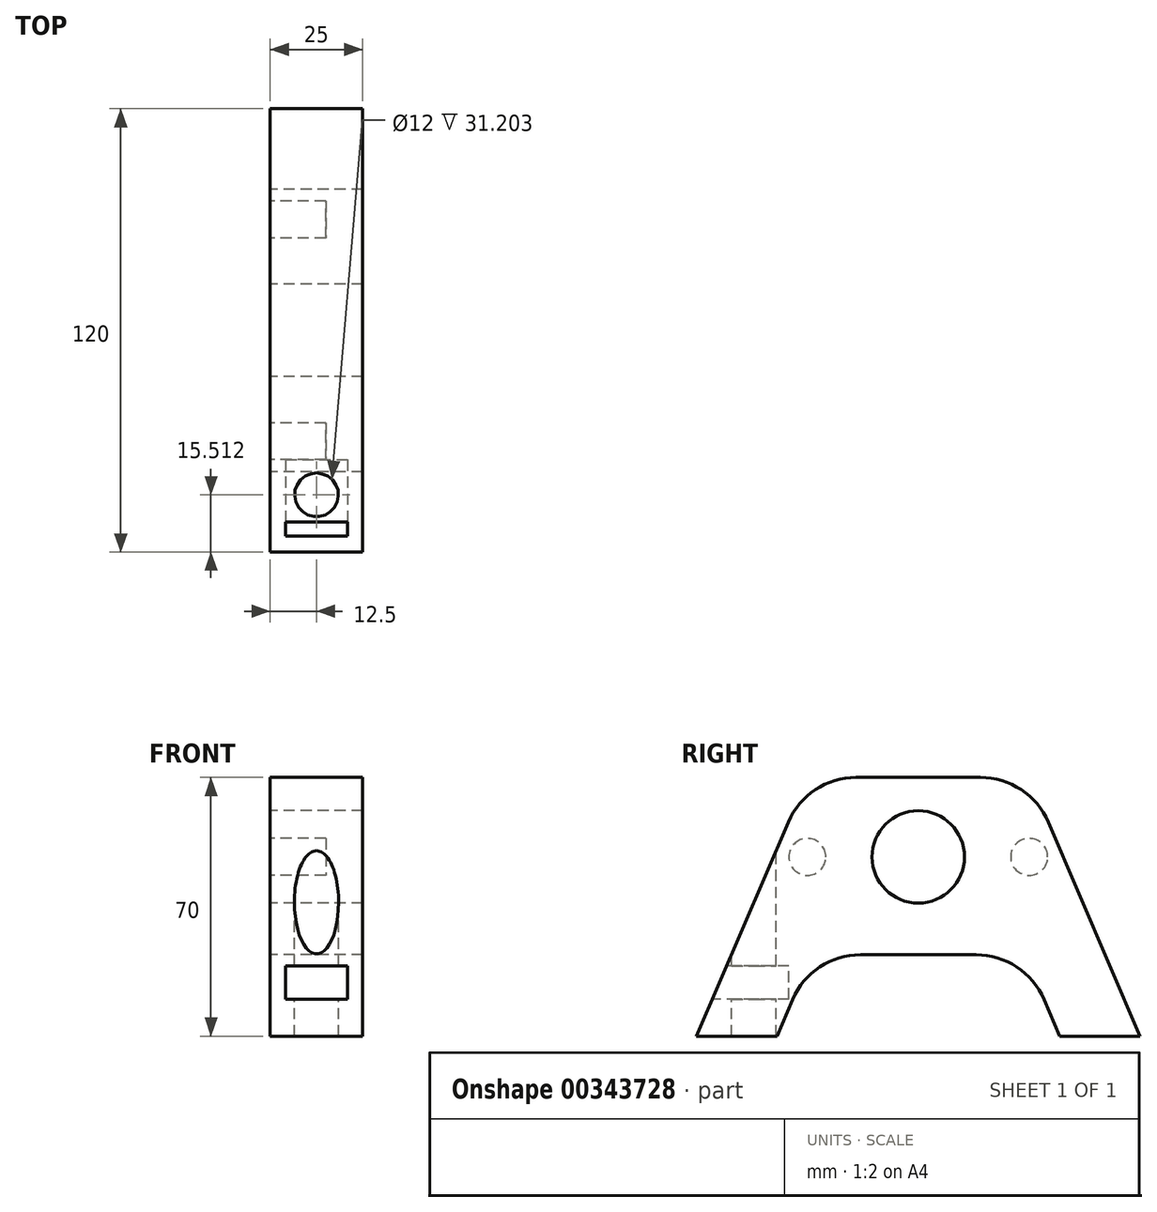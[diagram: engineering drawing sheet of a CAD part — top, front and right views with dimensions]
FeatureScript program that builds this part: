
annotation { "Feature Type Name" : "Feature", "Feature Type Description" : "" }
export const myFeature = defineFeature(function(context is Context, id is Id, definition is map)
    precondition{}
    {
        {
            var Q0;
            Q0=qCreatedBy(makeId("Right.planeOp"),FACE);
            var sketch = newSketch(context, id + "F0", { "sketchPlane" : qUnion([Q0])});
            skLineSegment(sketch, "E0.bottom", {"start": v(60, -35) * mm, "end": v(-60, -35) * mm});
            skLineSegment(sketch, "E0.top", {"start": v(60, 35) * mm, "end": v(-60, 35) * mm});
            skLineSegment(sketch, "E0.left", {"start": v(60, -35) * mm, "end": v(60, 35) * mm});
            skLineSegment(sketch, "E0.right", {"start": v(-60, -35) * mm, "end": v(-60, 35) * mm});
            skPoint(sketch, "E0.middle", {"position": v(0, 0) * mm});
            skLineSegment(sketch, "E1", {"start": v(-60, -35) * mm, "end": v(-30, 35) * mm});
            skLineSegment(sketch, "E2", {"start": v(60, -35) * mm, "end": v(30, 35) * mm});
            skSolve(sketch);
        }
        {
            var Q0;
            Q0=makeQuery(id+"F0.imprint","IMPRINT",FACE,{"disambiguationData":[TD([[makeQuery(id+"F0.imprint","IMPRINT",EDGE,{"derivedFrom":sQuery(id+"F0.wireOp",EDGE,"E0.bottom")}),-1.0]])]});
            extrude(context, id + "F1", {"entities" : qUnion([Q0]), "depth" : 25 * mm});
        }
        {
            var Q0;
            Q0=makeQuery(id+"F1.opExtrude","CAP_FACE",FACE,{"disambiguationData":[OSD([sQuery(id+"F0.wireOp",EDGE,"E0.bottom"),sQuery(id+"F0.wireOp",EDGE,"E0.top"),sQuery(id+"F0.wireOp",EDGE,"E1"),sQuery(id+"F0.wireOp",EDGE,"E2")])],"isStart":true});
            var sketch = newSketch(context, id + "F2", { "sketchPlane" : qUnion([Q0])});
            skCircle(sketch, "E3", {"center": v(-30, 13.5) * mm, "radius": 5 * mm});
            skCircle(sketch, "E4", {"center": v(30, 13.5) * mm, "radius": 5 * mm});
            skCircle(sketch, "E5.0", {"center": v(0, 13.5) * mm, "radius": 12.5 * mm});
            skSolve(sketch);
        }
        {
            var Q0;
            Q0=makeQuery(id+"F2.imprint","IMPRINT",FACE,{"disambiguationData":[TD([[makeQuery(id+"F2.imprint","IMPRINT",EDGE,{"derivedFrom":sQuery(id+"F2.wireOp",EDGE,"E3")}),1.0]])]});
            var Q1;
            Q1=makeQuery(id+"F2.imprint","IMPRINT",FACE,{"disambiguationData":[TD([[makeQuery(id+"F2.imprint","IMPRINT",EDGE,{"derivedFrom":sQuery(id+"F2.wireOp",EDGE,"E4")}),1.0]])]});
            extrude(context, id + "F3", {"entities" : qUnion([Q0, Q1]), "operationType" : NewBodyOperationType.REMOVE, "oppositeDirection" : true, "depth" : 15 * mm});
        }
        {
            var Q0;
            Q0=makeQuery(id+"F1.opExtrude","CAP_FACE",FACE,{"disambiguationData":[OSD([sQuery(id+"F0.wireOp",EDGE,"E0.bottom"),sQuery(id+"F0.wireOp",EDGE,"E0.top"),sQuery(id+"F0.wireOp",EDGE,"E1"),sQuery(id+"F0.wireOp",EDGE,"E2")])],"isStart":true});
            var sketch = newSketch(context, id + "F4", { "sketchPlane" : qUnion([Q0])});
            skLineSegment(sketch, "E6.0", {"start": v(-41.62, -42.88) * mm, "end": v(-11.62, 27.12) * mm});
            skLineSegment(sketch, "E7.0", {"start": v(41.62, -42.88) * mm, "end": v(11.62, 27.12) * mm});
            skLineSegment(sketch, "E8", {"start": v(-28.81, -13) * mm, "end": v(28.81, -13) * mm});
            skSolve(sketch);
        }
        {
            var Q0;
            {var subQ0=sQuery(id+"F4.wireOp",EDGE,"E8");Q0=makeQuery(id+"F4.imprint","IMPRINT",FACE,{"disambiguationData":[TD([[makeQuery(id+"F4.imprint","IMPRINT",EDGE,{"derivedFrom":subQ0}),-1.0]])]});}
            extrude(context, id + "F5", {"entities" : qUnion([Q0]), "operationType" : NewBodyOperationType.REMOVE, "oppositeDirection" : true, "depth" : 25 * mm});
        }
        {
            var Q0;
            Q0=qCreatedBy(makeId("Front.planeOp"),FACE);
            cPlane(context, id + "F6", {"entities" : qUnion([Q0]), "cplaneType" : CPlaneType.OFFSET, "offset" : 60 * mm, "width" : 150 * mm, "height" : 150 * mm});
        }
        {
            var Q0;
            Q0=qCreatedBy(id+"F6.planeOp",FACE);
            var sketch = newSketch(context, id + "F7", { "sketchPlane" : qUnion([Q0])});
            skLineSegment(sketch, "E9.bottom", {"start": v(4.13, -25) * mm, "end": v(20.88, -25) * mm});
            skLineSegment(sketch, "E9.top", {"start": v(4.13, -16) * mm, "end": v(20.88, -16) * mm});
            skLineSegment(sketch, "E9.left", {"start": v(4.13, -25) * mm, "end": v(4.13, -16) * mm});
            skLineSegment(sketch, "E9.right", {"start": v(20.88, -25) * mm, "end": v(20.88, -16) * mm});
            skPoint(sketch, "E10", {"position": v(12.5, -16) * mm});
            skSolve(sketch);
        }
        {
            var Q0;
            Q0=qSketchRegion(id+"F7",true);
            extrude(context, id + "F8", {"entities" : qUnion([Q0]), "operationType" : NewBodyOperationType.REMOVE, "oppositeDirection" : true, "depth" : 25 * mm});
        }
        {
            var Q0;
            Q0=makeQuery(id+"F8.boolean.opBoolean","COPY",FACE,{"derivedFrom":makeQuery(id+"F8.opExtrude","SWEPT_FACE",FACE,{"disambiguationData":[OSD([sQuery(id+"F7.wireOp",EDGE,"E9.bottom")])]})});
            var sketch = newSketch(context, id + "F9", { "sketchPlane" : qUnion([Q0])});
            skLineSegment(sketch, "E11.bottom", {"start": v(4.13, -35) * mm, "end": v(20.88, -35) * mm});
            skLineSegment(sketch, "E11.top", {"start": v(4.13, -51.75) * mm, "end": v(20.88, -51.75) * mm});
            skLineSegment(sketch, "E11.left", {"start": v(4.13, -35) * mm, "end": v(4.13, -51.75) * mm});
            skLineSegment(sketch, "E11.right", {"start": v(20.88, -35) * mm, "end": v(20.88, -51.75) * mm});
            skCircle(sketch, "E12.cCircle", {"center": v(12.5, -44.49) * mm, "radius": 8 * mm, "construction": true});
            skPoint(sketch, "E12.cCircle.perimeterSnap0", {"position": v(20.88, -43.38) * mm});
            skLineSegment(sketch, "E12.0", {"start": v(20.5, -39.87) * mm, "end": v(20.5, -49.1) * mm});
            skLineSegment(sketch, "E12.1", {"start": v(20.5, -49.1) * mm, "end": v(12.5, -53.73) * mm});
            skLineSegment(sketch, "E12.2", {"start": v(12.5, -53.73) * mm, "end": v(4.5, -49.1) * mm});
            skLineSegment(sketch, "E12.3", {"start": v(4.5, -49.1) * mm, "end": v(4.5, -39.87) * mm});
            skLineSegment(sketch, "E12.4", {"start": v(4.5, -39.87) * mm, "end": v(12.5, -35.25) * mm});
            skLineSegment(sketch, "E12.5", {"start": v(12.5, -35.25) * mm, "end": v(20.5, -39.87) * mm});
            skPoint(sketch, "E12.0.midPoint", {"position": v(20.42, -43.38) * mm});
            skPoint(sketch, "E12.0.midPoint.positionSnap0", {"position": v(20.88, -43.38) * mm});
            skCircle(sketch, "E13", {"center": v(12.5, -44.49) * mm, "radius": 6 * mm});
            skSolve(sketch);
        }
        {
            var Q0;
            Q0=makeQuery(id+"F9.imprint","IMPRINT",FACE,{"disambiguationData":[TD([[makeQuery(id+"F9.imprint","IMPRINT",EDGE,{"derivedFrom":sQuery(id+"F9.wireOp",EDGE,"E13")}),1.0]])]});
            extrude(context, id + "F10", {"entities" : qUnion([Q0]), "operationType" : NewBodyOperationType.REMOVE, "oppositeDirection" : true, "depth" : 100 * mm, "symmetric" : true});
        }
        {
            var Q0;
            Q0=makeQuery(id+"F5.boolean.opBoolean","COPY",EDGE,{"derivedFrom":makeQuery(id+"F5.opExtrude","SWEPT_EDGE",EDGE,{"disambiguationData":[OSD([sQuery(id+"F4.wireOp",EDGE,"E7.0"),sQuery(id+"F4.wireOp",EDGE,"E8")])]})});
            var Q1;
            Q1=makeQuery(id+"F5.boolean.opBoolean","COPY",EDGE,{"derivedFrom":makeQuery(id+"F5.opExtrude","SWEPT_EDGE",EDGE,{"disambiguationData":[OSD([sQuery(id+"F4.wireOp",EDGE,"E6.0"),sQuery(id+"F4.wireOp",EDGE,"E8")])]})});
            var Q2;
            Q2=makeQuery(id+"F1.opExtrude","SWEPT_EDGE",EDGE,{"disambiguationData":[OSD([sQuery(id+"F0.wireOp",EDGE,"E0.top"),sQuery(id+"F0.wireOp",EDGE,"E2")])]});
            var Q3;
            Q3=makeQuery(id+"F1.opExtrude","SWEPT_EDGE",EDGE,{"disambiguationData":[OSD([sQuery(id+"F0.wireOp",EDGE,"E0.top"),sQuery(id+"F0.wireOp",EDGE,"E1")])]});
            fillet(context, id + "F11", {"entities" : qUnion([Q0, Q1, Q2, Q3]), "radius" : 20 * mm, "tangentPropagation" : true, "allowEdgeOverflow" : false});
        }
        {
            var Q0;
            Q0=makeQuery(id+"F2.imprint","IMPRINT",FACE,{"disambiguationData":[TD([[makeQuery(id+"F2.imprint","IMPRINT",EDGE,{"derivedFrom":sQuery(id+"F2.wireOp",EDGE,"E5.0")}),1.0]])]});
            extrude(context, id + "F12", {"entities" : qUnion([Q0]), "operationType" : NewBodyOperationType.REMOVE, "oppositeDirection" : true, "depth" : 25 * mm});
        }
    });
